# Revit family: PG
name_source: partatom
category: Lighting Fixtures
units: mm (PartAtom-declared; Revit-internal decimal feet)

## family parameters
Cut with Voids When Loaded = No
Host = Face
Light Source = Yes
OmniClass Number = 23.80.70.11
OmniClass Title = Luminaries for Internal Lighting
Part Type = Normal
Room Calculation Point = No
Round Connector Dimension = Use Diameter
Shared = Yes

## types (4) — shared parameters
Apparent Load = 0 VA
Color Filter = 16777215
Default Elevation = 48 "
Description = Wet location listed emergency lighting unit for indoor/outdoor installation featuring long-life, high-output LEDs.
Dimming Lamp Color Temperature Shift = <None>
Emit from Line Length = 24 "
Lens = White Glass
Manufacturer = Dual Lighting
Model = PG
Total Input Wattage = 2-16 W
URL = https://www.currentlighting.com
Voltage = 120 V

## per-type parameters (varying)
| type | Finish | Photometric Web File | Tilt Angle |
| PG-W | White | generic | 60.00° |
| PG-Z | Bronze | generic | 60.00° |
| PG-P | Platinum Silver | pg_series.ies | 0.00° |
| PG-B | Black | generic | 60.00° |

## geometry (parser evidence)
native form markers: Blend x4, Sweep x2
no freeform markers — native parametric forms only
